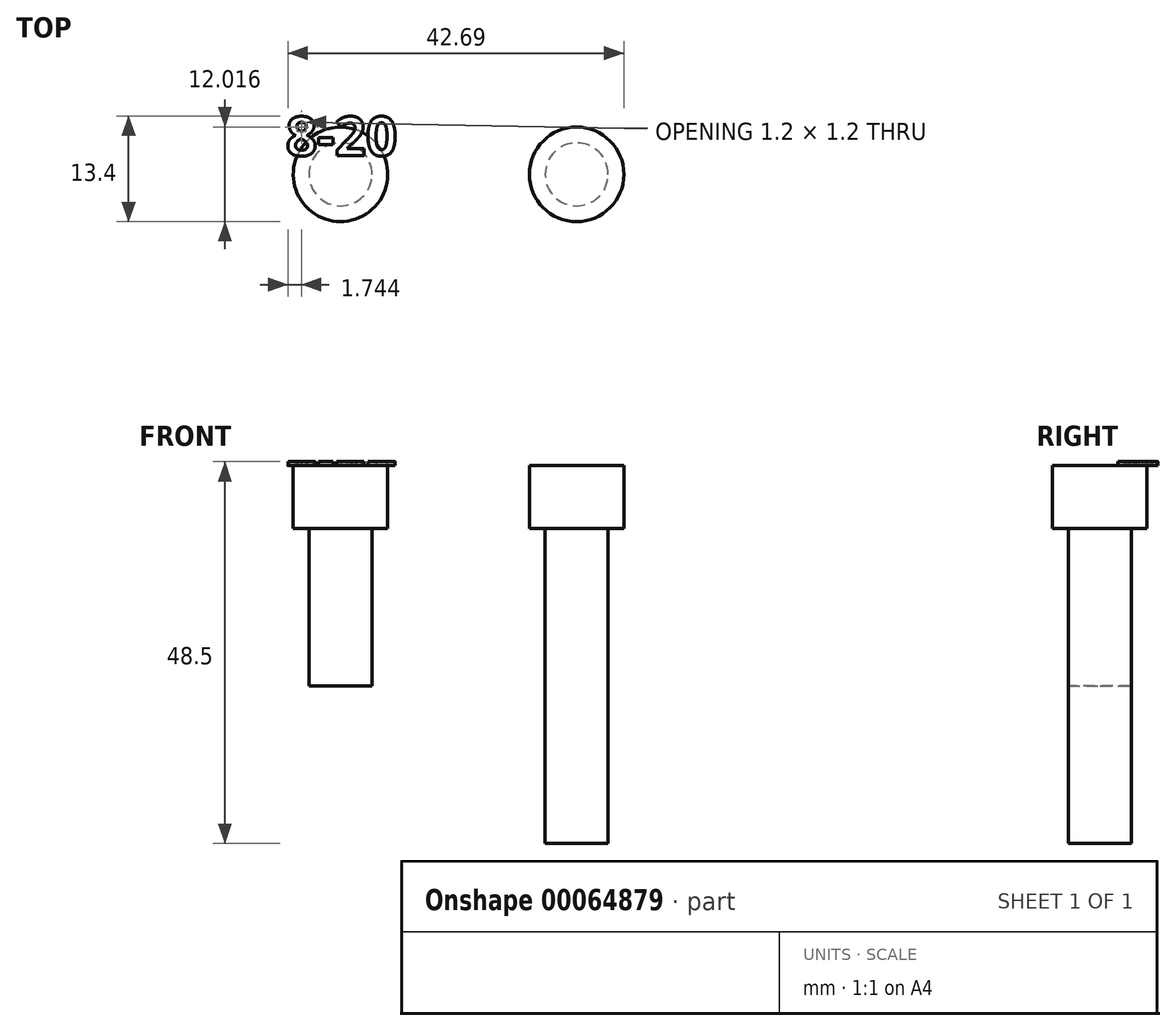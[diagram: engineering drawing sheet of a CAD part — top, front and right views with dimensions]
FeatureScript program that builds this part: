
annotation { "Feature Type Name" : "Feature", "Feature Type Description" : "" }
export const myFeature = defineFeature(function(context is Context, id is Id, definition is map)
    precondition{}
    {
        {
            var Q0;
            Q0=qCreatedBy(makeId("Top.planeOp"),FACE);
            var sketch = newSketch(context, id + "F0", { "sketchPlane" : qUnion([Q0])});
            skCircle(sketch, "E0", {"center": v(0, 0) * mm, "radius": 4 * mm});
            skSolve(sketch);
        }
        {
            var Q0;
            Q0=qSketchRegion(id+"F0",true);
            extrude(context, id + "F1", {"entities" : qUnion([Q0]), "depth" : 20 * mm});
        }
        {
            var Q0;
            Q0=makeQuery(id+"F1.opExtrude","CAP_FACE",FACE,{"disambiguationData":[OSD([sQuery(id+"F0.wireOp",EDGE,"E0")])],"isStart":false});
            var sketch = newSketch(context, id + "F2", { "sketchPlane" : qUnion([Q0])});
            skCircle(sketch, "E1", {"center": v(0, 0) * mm, "radius": 6 * mm});
            skSolve(sketch);
        }
        {
            var Q0;
            Q0=qSketchRegion(id+"F2",true);
            extrude(context, id + "F3", {"entities" : qUnion([Q0]), "operationType" : NewBodyOperationType.ADD, "depth" : 8 * mm});
        }
        {
            var Q0;
            Q0=makeQuery(id+"F3.opExtrude","CAP_FACE",FACE,{"disambiguationData":[OSD([sQuery(id+"F2.wireOp",EDGE,"E1")])],"isStart":false});
            var sketch = newSketch(context, id + "F4", { "sketchPlane" : qUnion([Q0]), "asVersion" : FeatureScriptVersionNumber.V307_HOLE_FEATURE_FIX_UNDETERMINED_TARGET_BODY_2});
            skText(sketch, "E2", { "text": "8-20", "fontName": "OpenSans-Bold.ttf"});
            const initialGuessF4  = {"E2": [-0.00693, 0.00236, 1, 0, 0.005]};
            skSetInitialGuess(sketch, initialGuessF4);
            skSolve(sketch);
        }
        {
            var Q0;
            Q0=makeQuery(id+"F1.opExtrude","SWEPT_BODY",BODY,{"disambiguationData":[OSD([sQuery(id+"F0.wireOp",EDGE,"E0")])]});
            transform(context, id + "F5", {"entities" : qUnion([Q0]), "transformType" : TransformType.TRANSLATION_3D, "dx" : 30 * mm, "dy" : 0 * mm, "dz" : 0 * mm, "makeCopy" : true});
        }
        {
            var Q0;
            Q0=makeQuery(id+"F5.opPattern","COPY",FACE,{"derivedFrom":makeQuery(id+"F1.opExtrude","CAP_FACE",FACE,{"disambiguationData":[OSD([sQuery(id+"F0.wireOp",EDGE,"E0")])],"isStart":true}),"instanceName":"1"});
            extrude(context, id + "F6", {"entities" : qUnion([Q0]), "operationType" : NewBodyOperationType.ADD, "depth" : 20 * mm});
        }
        {
            var Q0;
            Q0=qSketchRegion(id+"F4",true);
            extrude(context, id + "F7", {"entities" : qUnion([Q0]), "operationType" : NewBodyOperationType.ADD, "depth" : 0.5 * mm});
        }
    });
